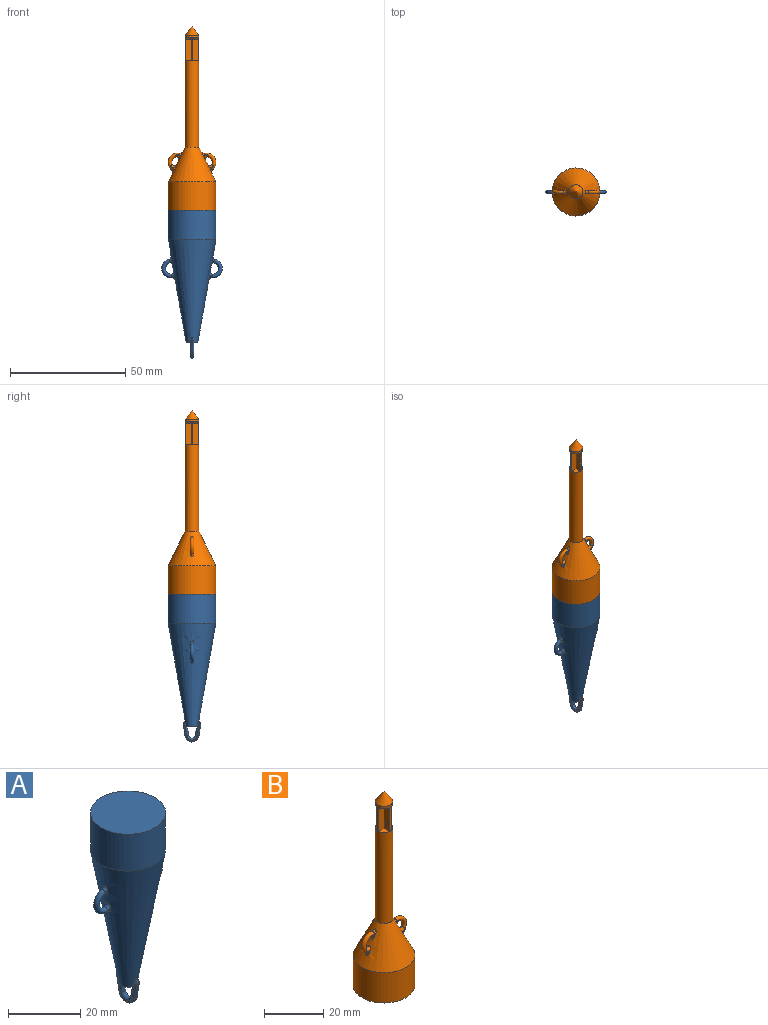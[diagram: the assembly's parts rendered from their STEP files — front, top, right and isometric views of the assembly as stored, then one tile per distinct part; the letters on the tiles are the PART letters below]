
ASSEMBLY  parts=2 mates=1
PART A: 46 faces, bbox 27x20.9x64.4 mm
  f0: plane 1.29x0.65mm, normal (0,1,0), area 0.2mm2, adj f6,f24,f27,f28
  f1: plane 1.31x0.66mm, normal (0,-1,0), area 0.2mm2, adj f6,f25,f26,f27
  f2: plane 1.31x0.66mm, normal (0,1,0), area 0.2mm2, adj f6,f19,f20,f22
  f3: plane 1.29x0.65mm, normal (0,-1,0), area 0.2mm2, adj f6,f21,f22,f23
  f4: plane 20.8x20.8mm, normal (0,0,1), area 339.8mm2, adj f7
  f5: plane 5.12x4.95mm, normal (0,0,-1), area 18.8mm2, adj f6,f29,f31
  f6: cone r=10.4mm half-angle=10deg, axis (0,0,1), area 1828.8mm2, adj f0,f1,f2,f3,f5,f7,f13,f14
  f7: cylinder r=10.4mm len=20.8mm, axis (0,0,1), area 816.8mm2, adj f4,f6
  f8: plane 5.07x0.89mm, normal (0,-0.98,-0.17), area 4.2mm2, adj f9,f13,f36,f43
  f9: cylinder r=3.02mm len=5.95mm, axis (-1,0,0), area 6.9mm2, adj f8,f10,f35,f42
  f10: plane 5.07x0.89mm, normal (0,0.98,-0.17), area 4.2mm2, adj f9,f14,f34,f41
  f11: plane 8.01x6.99mm, normal (1,0,0), area 7.4mm2, adj f29,f30,f31,f40,f41,f42,f43,f44
  f12: plane 8.01x6.99mm, normal (-1,0,0), area 7.4mm2, adj f29,f30,f31,f33,f34,f35,f36,f37
  f13: bspline ~1.39x1.2mm, area 1.4mm2, adj f6,f8,f37,f38,f44,f45
  f14: bspline ~1.42x1.4mm, area 1.4mm2, adj f6,f10,f32,f33,f39,f40
  f15: plane 1.31x0.66mm, normal (0,-1,0), area 0.2mm2, adj f6,f19,f20,f22
  f16: plane 1.29x0.65mm, normal (0,1,0), area 0.2mm2, adj f6,f21,f22,f23
  f17: plane 1.29x0.65mm, normal (0,-1,0), area 0.2mm2, adj f6,f24,f27,f28
  f18: plane 1.31x0.66mm, normal (0,1,0), area 0.2mm2, adj f6,f25,f26,f27
  f19: torus R=1.8mm, axis (0,-1,0), area 3.3mm2, adj f2,f6,f15,f22
  f20: torus R=1.8mm, axis (0,-1,0), area 3.8mm2, adj f2,f6,f15,f22
  f21: torus R=1.8mm, axis (0,-1,0), area 3.3mm2, adj f3,f6,f16,f22
  f22: torus R=3.3mm, axis (0,-1,0), area 49.7mm2, adj f2,f3,f15,f16,f19,f20,f21,f23
  f23: torus R=1.8mm, axis (0,-1,0), area 3.8mm2, adj f3,f6,f16,f22
  f24: torus R=1.8mm, axis (0,-1,0), area 3.3mm2, adj f0,f6,f17,f27
  f25: torus R=1.8mm, axis (0,-1,0), area 3.3mm2, adj f1,f6,f18,f27
  f26: torus R=1.8mm, axis (0,-1,0), area 3.8mm2, adj f1,f6,f18,f27
  f27: torus R=3.3mm, axis (0,-1,0), area 49.7mm2, adj f0,f1,f17,f18,f24,f25,f26,f28
  f28: torus R=1.8mm, axis (0,-1,0), area 3.8mm2, adj f0,f6,f17,f27
  f29: cylinder r=0.8mm len=6.06mm, axis (0,0.17,0.98), area 11.8mm2, adj f5,f6,f11,f12,f30,f32,f39
  f30: torus R=2.22mm, axis (1,0,0), area 11.8mm2, adj f11,f12,f29,f31
  f31: cylinder r=0.8mm len=5.98mm, axis (0,0.17,-0.98), area 11.6mm2, adj f5,f6,f11,f12,f30,f38,f45
  f32: bspline ~1.07x0.71mm, area 0.4mm2, adj f6,f14,f29,f33
  f33: bspline ~1.4x0.77mm, area 0.7mm2, adj f12,f14,f32,f34
  f34: cylinder r=0.39mm len=5.13mm, axis (0,0.17,0.98), area 3.2mm2, adj f10,f12,f33,f35
  f35: torus R=2.63mm, axis (1,0,0), area 4.9mm2, adj f9,f12,f34,f36
  f36: cylinder r=0.39mm len=5.13mm, axis (0,0.17,-0.98), area 3.2mm2, adj f8,f12,f35,f37
  f37: bspline ~1.35x0.76mm, area 0.7mm2, adj f12,f13,f36,f38
  f38: bspline ~1.18x0.73mm, area 0.4mm2, adj f6,f13,f31,f37
  f39: bspline ~1.07x0.71mm, area 0.4mm2, adj f6,f14,f29,f40
  f40: bspline ~1.4x0.77mm, area 0.7mm2, adj f11,f14,f39,f41
  f41: cylinder r=0.39mm len=5.13mm, axis (0,-0.17,-0.98), area 3.2mm2, adj f10,f11,f40,f42
  f42: torus R=2.63mm, axis (1,0,0), area 4.9mm2, adj f9,f11,f41,f43
  f43: cylinder r=0.39mm len=5.13mm, axis (0,-0.17,0.98), area 3.2mm2, adj f8,f11,f42,f44
  f44: bspline ~1.35x0.76mm, area 0.7mm2, adj f11,f13,f43,f45
  f45: bspline ~1.18x0.73mm, area 0.4mm2, adj f6,f13,f31,f44
PART B: 68 faces, bbox 21.5x20.8x80 mm
  f0: plane 1.96x1.95mm, normal (0,1,0), area 0.6mm2, adj f16,f65,f66,f67
  f1: plane 2.52x1.02mm, normal (0,-1,0), area 0.6mm2, adj f16,f63,f64,f66
  f2: plane 1.96x1.95mm, normal (0,-1,0), area 0.6mm2, adj f16,f58,f61,f62
  f3: plane 2.52x1.02mm, normal (0,1,0), area 0.6mm2, adj f16,f59,f60,f61
  f4: plane 0.4x0.03mm, normal (0,0,1), area 0mm2, adj f31,f42,f48
  f5: plane 0.4x0.03mm, normal (0,0,1), area 0mm2, adj f31,f32,f48
  f6: plane 0.4x0.03mm, normal (0,0,1), area 0mm2, adj f33,f34,f48
  f7: plane 0.4x0.03mm, normal (0,0,1), area 0mm2, adj f34,f35,f48
  f8: plane 0.4x0.03mm, normal (0,0,1), area 0mm2, adj f36,f37,f48
  f9: plane 0.4x0.03mm, normal (0,0,1), area 0mm2, adj f37,f38,f48
  f10: plane 0.4x0.03mm, normal (0,0,1), area 0mm2, adj f40,f41,f48
  f11: plane 2.57x2.57mm, normal (0,0,1), area 4.8mm2, adj f17,f38,f39
  f12: plane 2.57x2.57mm, normal (0,0,1), area 4.8mm2, adj f17,f35,f36
  f13: plane 2.57x2.57mm, normal (0,0,1), area 4.8mm2, adj f17,f41,f42
  f14: plane 20.8x20.8mm, normal (0,0,-1), area 339.8mm2, adj f15
  f15: cylinder r=10.4mm len=20.8mm, axis (0,0,1), area 816.8mm2, adj f14,f16
  f16: cone r=10.4mm half-angle=26.3deg, axis (0,0,-1), area 686.9mm2, adj f0,f1,f2,f3,f15,f17,f19,f20
  f17: cylinder r=3mm len=37.5mm, axis (0,0,1), area 706.9mm2, adj f11,f12,f13,f16,f18,f23,f24,f25
  f18: plane 2.57x2.57mm, normal (0,0,1), area 4.8mm2, adj f17,f32,f33
  f19: plane 2.52x1.02mm, normal (0,-1,0), area 0.6mm2, adj f16,f59,f60,f61
  f20: plane 1.96x1.95mm, normal (0,1,0), area 0.6mm2, adj f16,f58,f61,f62
  f21: plane 1.96x1.95mm, normal (0,-1,0), area 0.6mm2, adj f16,f65,f66,f67
  f22: plane 2.52x1.02mm, normal (0,1,0), area 0.6mm2, adj f16,f63,f64,f66
  f23: plane 0.4x0.03mm, normal (0,0,-1), area 0mm2, adj f17,f31,f42
  f24: plane 0.4x0.03mm, normal (0,0,-1), area 0mm2, adj f17,f31,f32
  f25: plane 0.4x0.03mm, normal (0,0,-1), area 0mm2, adj f17,f33,f34
  f26: plane 0.4x0.03mm, normal (0,0,-1), area 0mm2, adj f17,f34,f35
  f27: plane 0.4x0.03mm, normal (0,0,-1), area 0mm2, adj f17,f36,f37
  f28: plane 0.4x0.03mm, normal (0,0,-1), area 0mm2, adj f17,f37,f38
  f29: plane 0.4x0.03mm, normal (0,0,-1), area 0mm2, adj f17,f40,f41
  f30: plane 0.4x0.03mm, normal (0,0,-1), area 0mm2, adj f17,f39,f40
  f31: plane 10x0.8mm, normal (0,1,0), area 8mm2, adj f4,f5,f23,f24,f32,f42
  f32: plane 10x2.6mm, normal (-1,0,0), area 23.4mm2, adj f5,f18,f24,f31,f33,f48,f54
  f33: plane 10x2.6mm, normal (0,1,0), area 23.4mm2, adj f6,f18,f25,f32,f34,f48,f55
  f34: plane 10x0.8mm, normal (-1,0,0), area 8mm2, adj f6,f7,f25,f26,f33,f35
  f35: plane 10x2.6mm, normal (0,-1,0), area 23.4mm2, adj f7,f12,f26,f34,f36,f48,f53
  f36: plane 10x2.6mm, normal (-1,0,0), area 23.4mm2, adj f8,f12,f27,f35,f37,f48,f52
  f37: plane 10x0.8mm, normal (0,-1,0), area 8mm2, adj f8,f9,f27,f28,f36,f38
  f38: plane 10x2.6mm, normal (1,0,0), area 23.4mm2, adj f9,f11,f28,f37,f39,f48,f57
  f39: plane 10x2.6mm, normal (0,-1,0), area 23.4mm2, adj f11,f30,f38,f40,f43,f48,f56
  f40: plane 10x0.8mm, normal (1,0,0), area 8mm2, adj f10,f29,f30,f39,f41,f43
  f41: plane 10x2.6mm, normal (0,1,0), area 23.4mm2, adj f10,f13,f29,f40,f42,f48,f50
  f42: plane 10x2.6mm, normal (1,0,0), area 23.4mm2, adj f4,f13,f23,f31,f41,f48,f51
  f43: plane 0.4x0.03mm, normal (0,0,1), area 0mm2, adj f39,f40,f48
  f44: plane 1.25x1.25mm, normal (0,0,-1), area 0.9mm2, adj f48,f54,f55
  f45: plane 1.25x1.25mm, normal (0,0,-1), area 0.9mm2, adj f48,f52,f53
  f46: plane 1.25x1.25mm, normal (0,0,-1), area 0.9mm2, adj f48,f56,f57
  f47: plane 1.25x1.25mm, normal (0,0,-1), area 0.9mm2, adj f48,f50,f51
  f48: cylinder r=3mm len=6mm, axis (0,0,1), area 16.8mm2, adj f4,f5,f6,f7,f8,f9,f10,f32
  f49: cone r=3mm half-angle=35.5deg, axis (0,0,-1), area 48.6mm2, adj f48
  f50: cylinder r=1mm len=2.57mm, axis (1,0,0), area 3mm2, adj f41,f47,f48,f51
  f51: cylinder r=1mm len=2.57mm, axis (0,-1,0), area 3mm2, adj f42,f47,f48,f50
  f52: cylinder r=1mm len=2.57mm, axis (0,1,0), area 3mm2, adj f36,f45,f48,f53
  f53: cylinder r=1mm len=2.57mm, axis (-1,0,0), area 3mm2, adj f35,f45,f48,f52
  f54: cylinder r=1mm len=2.57mm, axis (0,1,0), area 3mm2, adj f32,f44,f48,f55
  f55: cylinder r=1mm len=2.57mm, axis (1,0,0), area 3mm2, adj f33,f44,f48,f54
  f56: cylinder r=1mm len=2.57mm, axis (-1,0,0), area 3mm2, adj f39,f46,f48,f57
  f57: cylinder r=1mm len=2.57mm, axis (0,-1,0), area 3mm2, adj f38,f46,f48,f56
  f58: torus R=1.8mm, axis (0,-1,0), area 2.7mm2, adj f2,f16,f20,f61
  f59: torus R=1.8mm, axis (0,-1,0), area 2.8mm2, adj f3,f16,f19,f61
  f60: torus R=1.8mm, axis (0,-1,0), area 5.8mm2, adj f3,f16,f19,f61
  f61: torus R=3.3mm, axis (0,-1,0), area 38mm2, adj f2,f3,f19,f20,f58,f59,f60,f62
  f62: torus R=1.8mm, axis (0,-1,0), area 5.8mm2, adj f2,f16,f20,f61
  f63: torus R=1.8mm, axis (0,-1,0), area 5.8mm2, adj f1,f16,f22,f66
  f64: torus R=1.8mm, axis (0,-1,0), area 2.8mm2, adj f1,f16,f22,f66
  f65: torus R=1.8mm, axis (0,-1,0), area 5.8mm2, adj f0,f16,f21,f66
  f66: torus R=3.3mm, axis (0,-1,0), area 38mm2, adj f0,f1,f21,f22,f63,f64,f65,f67
  f67: torus R=1.8mm, axis (0,-1,0), area 2.7mm2, adj f0,f16,f21,f66
PLACE A t=(-0.07,0.13,38.56)mm fixed
PLACE B t=(-0.07,0.13,38.56)mm
MATE parallel B.f15 <-> A.f6  axis (0,0,-1) through (-0.07,0.13,38.56)mm
